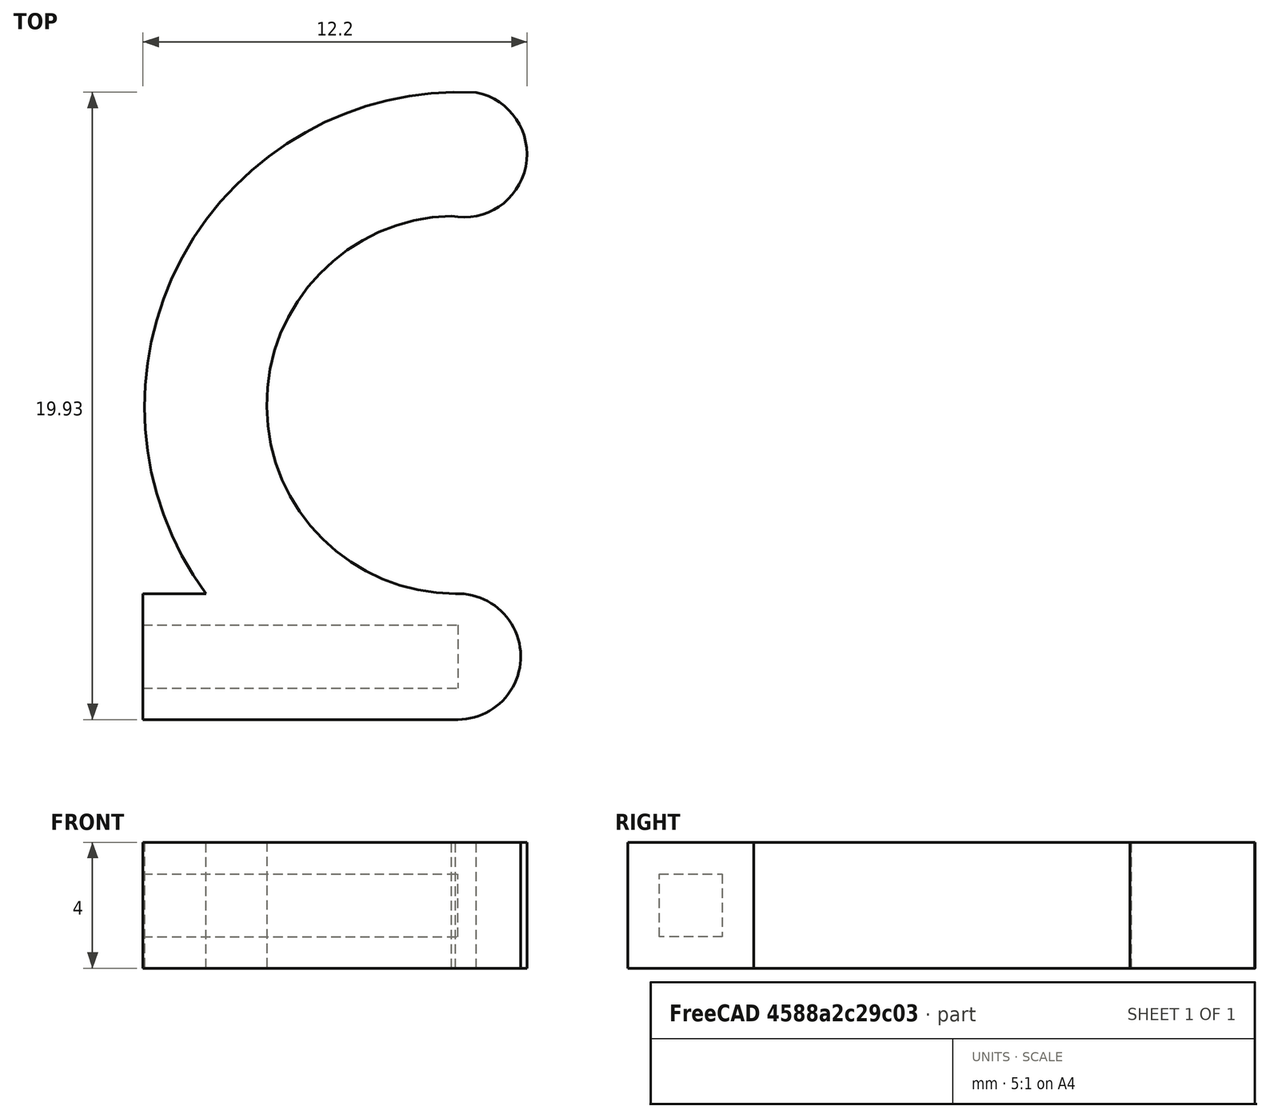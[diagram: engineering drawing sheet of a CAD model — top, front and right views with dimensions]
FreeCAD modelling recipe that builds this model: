
FCSTD DOCUMENT  (FreeCAD 0.18.1R)
Label: shub2R
License: All rights reserved
LicenseURL: http://en.wikipedia.org/wiki/All_rights_reserved
objects: TechDraw::DrawViewDimension×13, TechDraw::DrawProjGroupItem×4, Sketcher::SketchObject×2, PartDesign::Pad×1, PartDesign::Plane×1, PartDesign::Pocket×1, PartDesign::Body×1, TechDraw::DrawSVGTemplate×1, TechDraw::DrawProjGroup×1, TechDraw::DrawPage×1
note: 8 computed .brp shape members not serialized (recipe doc carries the construction recipe); baked Part::Feature solids carry a one-line shape summary decoded from their .brp

FEATURE [Sketcher::SketchObject] Sketch
  MapMode = 5
  Support = -> [XY_Plane]
  sketch-geometry (7):
    g0: LineSegment StartX=2 StartY=4 StartZ=0 EndX=0 EndY=4 EndZ=0
    g1: LineSegment StartX=0 StartY=4 StartZ=0 EndX=0 EndY=0 EndZ=0
    g2: LineSegment StartX=0 StartY=0 StartZ=0 EndX=10 EndY=0 EndZ=0
    g3: ArcOfCircle CenterX=10 CenterY=2 CenterZ=0 NormalX=0 NormalY=0 NormalZ=1 AngleXU=0 Radius=2 StartAngle=4.71239 EndAngle=7.88889
    g4: ArcOfCircle CenterX=9.9302 CenterY=9.99878 CenterZ=0 NormalX=0 NormalY=0 NormalZ=1 AngleXU=0 Radius=6 StartAngle=1.59191 EndAngle=4.71239
    g5: ArcOfCircle CenterX=10.0491 CenterY=9.93398 CenterZ=0 NormalX=0 NormalY=0 NormalZ=1 AngleXU=0 Radius=10 StartAngle=1.51666 EndAngle=3.77687
    g6: ArcOfCircle CenterX=10.1968 CenterY=17.9584 CenterZ=0 NormalX=0 NormalY=0 NormalZ=1 AngleXU=0 Radius=2 StartAngle=4.51444 EndAngle=7.65603
  constraints (24):
    c: Horizontal(g0)
    c: Coincident(g0,g1)
    c: Vertical(g1)
    c: Coincident(g1,g2)
    c: Horizontal(g2)
    c: DistanceX(g0,g0) = 2
    c: DistanceY(g1,g1) = 4
    c: DistanceX(g2,g2) = 10
    c: DistanceY(g2,g3) = 2
    c: Coincident(g3,g2)
    c: Angle(g3) = 3.1765
    c: DistanceY(g3,g4) = 6
    c: Coincident(g4,g3)
    c: Coincident(g5,g0)
    c: Radius(g6) = 2
    c: Coincident(g6,g4)
    c: Coincident(g6,g5)
    c: Angle(g6) = 3.14159
    c: Coincident(g1,g-1)
    c: Radius(g4) = 6
    c: Radius(g5) = 10
    c: Radius(g3) = 2
    c: Angle(g4) = 3.12047
    c: Angle(g5) = 2.2602
FEATURE [PartDesign::Pad] Pad
  Length = 4
  Length2 = 100
  Profile = -> Sketch
  Refine = true
  Type = 0
FEATURE [PartDesign::Plane] DatumPlane
  Length = 34.8117
  MapMode = 5
  Placement = pos=(0,0,0) rot=(0.57735,-0.57735,-0.57735;2.0944rad)
  ResizeMode = 0
  Support = -> [Pad]
  Width = 24.8924
FEATURE [Sketcher::SketchObject] Sketch001
  ExternalGeometry = -> [Pad]
  MapMode = 5
  Placement = pos=(0,0,0) rot=(0.57735,-0.57735,-0.57735;2.0944rad)
  Support = -> [DatumPlane]
  sketch-geometry (4):
    g0: LineSegment StartX=-1.0018 StartY=2.99221 StartZ=0 EndX=-3.0018 EndY=2.99221 EndZ=0
    g1: LineSegment StartX=-3.0018 StartY=2.99221 StartZ=0 EndX=-3.0018 EndY=0.992215 EndZ=0
    g2: LineSegment StartX=-3.0018 StartY=0.992215 StartZ=0 EndX=-1.0018 EndY=0.992215 EndZ=0
    g3: LineSegment StartX=-1.0018 StartY=0.992215 StartZ=0 EndX=-1.0018 EndY=2.99221 EndZ=0
  constraints (12):
    c: Coincident(g0,g1)
    c: Coincident(g1,g2)
    c: Coincident(g2,g3)
    c: Coincident(g3,g0)
    c: Horizontal(g0)
    c: Horizontal(g2)
    c: Vertical(g1)
    c: Vertical(g3)
    c: DistanceX(g0,g0) = 2
    c: DistanceY(g3,g3) = 2
    c: Distance(g-1,g2) = 1.41
    c: Distance(g0,g-3) = 1.421
FEATURE [PartDesign::Pocket] Pocket
  BaseFeature = -> Pad
  Length = 10
  Length2 = 100
  Profile = -> Sketch001
  Refine = true
  Type = 0
FEATURE [PartDesign::Body] Body
  Group = -> [Sketch,Pad,DatumPlane,Sketch001,Pocket]
  Origin = -> Origin
  Tip = -> Pocket
FEATURE [TechDraw::DrawSVGTemplate] Template
  EditableTexts = Designed_by_Name=Designed by Name; Drawing_number=Drawing number; FC-Date=Date; FC-SC=Scale; FC-SH=Sheet; FC-Title=Title; Subtitle=Subtitle; Weight=Weight
  Height = 210
  Orientation = 1
  Width = 297
FEATURE [TechDraw::DrawProjGroupItem] ProjItem  label="Front"
  CoarseView = false
  Direction = (0,-1,0)
  Focus = 100
  HardHidden = false
  IsoCount = 0
  IsoHidden = false
  IsoVisible = false
  LockPosition = true
  Perspective = false
  Rotation = 0
  RotationVector = (1,0,0)
  Scale = 2
  ScaleType = 2
  SeamHidden = false
  SeamVisible = false
  SmoothHidden = false
  SmoothVisible = false
  Source = -> [Body]
  Type = 0
  X = 0
  Y = 0
FEATURE [TechDraw::DrawProjGroupItem] ProjItem001  label="Top"
  CoarseView = false
  Direction = (0,0,1)
  Focus = 100
  HardHidden = false
  IsoCount = 0
  IsoHidden = false
  IsoVisible = false
  LockPosition = false
  Perspective = false
  Rotation = 0
  RotationVector = (1,0,0)
  Scale = 2
  ScaleType = 2
  SeamHidden = false
  SeamVisible = false
  SmoothHidden = false
  SmoothVisible = false
  Source = -> [Body]
  Type = 4
  X = 0
  Y = -82.2233
FEATURE [TechDraw::DrawProjGroupItem] ProjItem002  label="FrontTopLeft"
  CoarseView = false
  Direction = (-1,-1,1)
  Focus = 100
  HardHidden = false
  IsoCount = 0
  IsoHidden = false
  IsoVisible = false
  LockPosition = false
  Perspective = false
  Rotation = 0
  RotationVector = (1,-1,0)
  Scale = 2
  ScaleType = 2
  SeamHidden = false
  SeamVisible = false
  SmoothHidden = false
  SmoothVisible = false
  Source = -> [Body]
  Type = 6
  X = 80.8382
  Y = -65.9486
FEATURE [TechDraw::DrawProjGroupItem] ProjItem003  label="Left"
  CoarseView = false
  Direction = (-1,-1e-16,0)
  Focus = 100
  HardHidden = false
  IsoCount = 0
  IsoHidden = false
  IsoVisible = false
  LockPosition = false
  Perspective = false
  Rotation = 0
  RotationVector = (1e-16,-1,0)
  Scale = 2
  ScaleType = 2
  SeamHidden = false
  SeamVisible = false
  SmoothHidden = false
  SmoothVisible = false
  Source = -> [Body]
  Type = 1
  X = 82.5696
  Y = 0
FEATURE [TechDraw::DrawProjGroup] ProjGroup
  Anchor = -> ProjItem
  AutoDistribute = true
  LockPosition = false
  ProjectionType = 0
  Rotation = 0
  Scale = 2
  ScaleType = 0
  Source = -> [Body]
  Views = -> [ProjItem,ProjItem001,ProjItem002,ProjItem003]
  X = 44.2034
  Y = 175.224
  spacingX = 15
  spacingY = 15
FEATURE [TechDraw::DrawViewDimension] Dimension
  Arbitrary = false
  FormatSpec = %.2f
  LockPosition = false
  MeasureType = 1
  OverTolerance = 0
  References2D = -> [ProjItem]
  Rotation = 0
  Scale = 2
  ScaleType = 0
  Type = 1
  UnderTolerance = 0
  X = -2.76051
  Y = 17.3744
FEATURE [TechDraw::DrawViewDimension] Dimension001
  Arbitrary = false
  FormatSpec = %.2f
  LockPosition = false
  MeasureType = 1
  OverTolerance = 0
  References2D = -> [ProjItem]
  Rotation = 0
  Scale = 2
  ScaleType = 0
  Type = 2
  UnderTolerance = 0
  X = -24.8358
  Y = -15.7385
FEATURE [TechDraw::DrawViewDimension] Dimension002
  Arbitrary = false
  FormatSpec = R%.2f
  LockPosition = false
  MeasureType = 1
  OverTolerance = 0
  References2D = -> [ProjItem001]
  Rotation = 0
  Scale = 2
  ScaleType = 0
  Type = 4
  UnderTolerance = 0
  X = 31.1643
  Y = -7.96422
FEATURE [TechDraw::DrawViewDimension] Dimension003
  Arbitrary = false
  FormatSpec = R%.2f
  LockPosition = false
  MeasureType = 1
  OverTolerance = 0
  References2D = -> [ProjItem001]
  Rotation = 0
  Scale = 2
  ScaleType = 0
  Type = 4
  UnderTolerance = 0
  X = 4.50152
  Y = 19.0449
FEATURE [TechDraw::DrawViewDimension] Dimension004
  Arbitrary = false
  FormatSpec = R%.2f
  LockPosition = false
  MeasureType = 1
  OverTolerance = 0
  References2D = -> [ProjItem001]
  Rotation = 0
  Scale = 2
  ScaleType = 0
  Type = 4
  UnderTolerance = 0
  X = 30.1255
  Y = 5.19406
FEATURE [TechDraw::DrawViewDimension] Dimension005
  Arbitrary = false
  FormatSpec = %.2f
  LockPosition = false
  MeasureType = 1
  OverTolerance = 0
  References2D = -> [ProjItem001]
  Rotation = 0
  Scale = 2
  ScaleType = 0
  Type = 1
  UnderTolerance = 0
  X = 0.979211
  Y = -38.0149
FEATURE [TechDraw::DrawViewDimension] Dimension006
  Arbitrary = false
  FormatSpec = %.2f
  LockPosition = false
  MeasureType = 1
  OverTolerance = 0
  References2D = -> [ProjItem001]
  Rotation = 0
  Scale = 2
  ScaleType = 0
  Type = 2
  UnderTolerance = 0
  X = -24.4507
  Y = 7.96145
FEATURE [TechDraw::DrawViewDimension] Dimension007
  Arbitrary = false
  FormatSpec = %.2f
  LockPosition = false
  MeasureType = 1
  OverTolerance = 0
  References2D = -> [ProjItem003]
  Rotation = 0
  Scale = 2
  ScaleType = 0
  Type = 1
  UnderTolerance = 0
  X = 1.36652
  Y = -18.1112
FEATURE [TechDraw::DrawViewDimension] Dimension008
  Arbitrary = false
  FormatSpec = %.2f
  LockPosition = false
  MeasureType = 1
  OverTolerance = 0
  References2D = -> [ProjItem003]
  Rotation = 0
  Scale = 2
  ScaleType = 0
  Type = 2
  UnderTolerance = 0
  X = -25.3568
  Y = -0.480931
FEATURE [TechDraw::DrawViewDimension] Dimension009
  Arbitrary = false
  FormatSpec = %.2f
  LockPosition = false
  MeasureType = 1
  OverTolerance = 0
  References2D = -> [ProjItem003]
  Rotation = 0
  Scale = 2
  ScaleType = 0
  Type = 1
  UnderTolerance = 0
  X = 23.4136
  Y = -11.4628
FEATURE [TechDraw::DrawViewDimension] Dimension010
  Arbitrary = false
  FormatSpec = %.2f
  LockPosition = false
  MeasureType = 1
  OverTolerance = 0
  References2D = -> [ProjItem003]
  Rotation = 0
  Scale = 2
  ScaleType = 0
  Type = 2
  UnderTolerance = 0
  X = 35.433
  Y = -10.9935
FEATURE [TechDraw::DrawViewDimension] Dimension011
  Arbitrary = false
  FormatSpec = %.2f
  LockPosition = false
  MeasureType = 1
  OverTolerance = 0
  References2D = -> [ProjItem001]
  Rotation = 0
  Scale = 2
  ScaleType = 0
  Type = 1
  UnderTolerance = 0
  X = -14.2366
  Y = 28.1757
FEATURE [TechDraw::DrawViewDimension] Dimension012
  Arbitrary = false
  FormatSpec = %.2f
  LockPosition = false
  MeasureType = 1
  OverTolerance = 0
  References2D = -> [ProjItem]
  Rotation = 0
  Scale = 2
  ScaleType = 0
  Type = 1
  UnderTolerance = 0
  X = 21.3455
  Y = -18.1394
FEATURE [TechDraw::DrawPage] Page
  KeepUpdated = true
  ProjectionType = 0
  Scale = 2
  Template = -> Template
  Views = -> [ProjGroup,Dimension,Dimension001,Dimension002,Dimension003,Dimension004,Dimension005,Dimension006,Dimension007,Dimension008,Dimension009,Dimension010,Dimension011,Dimension012]
